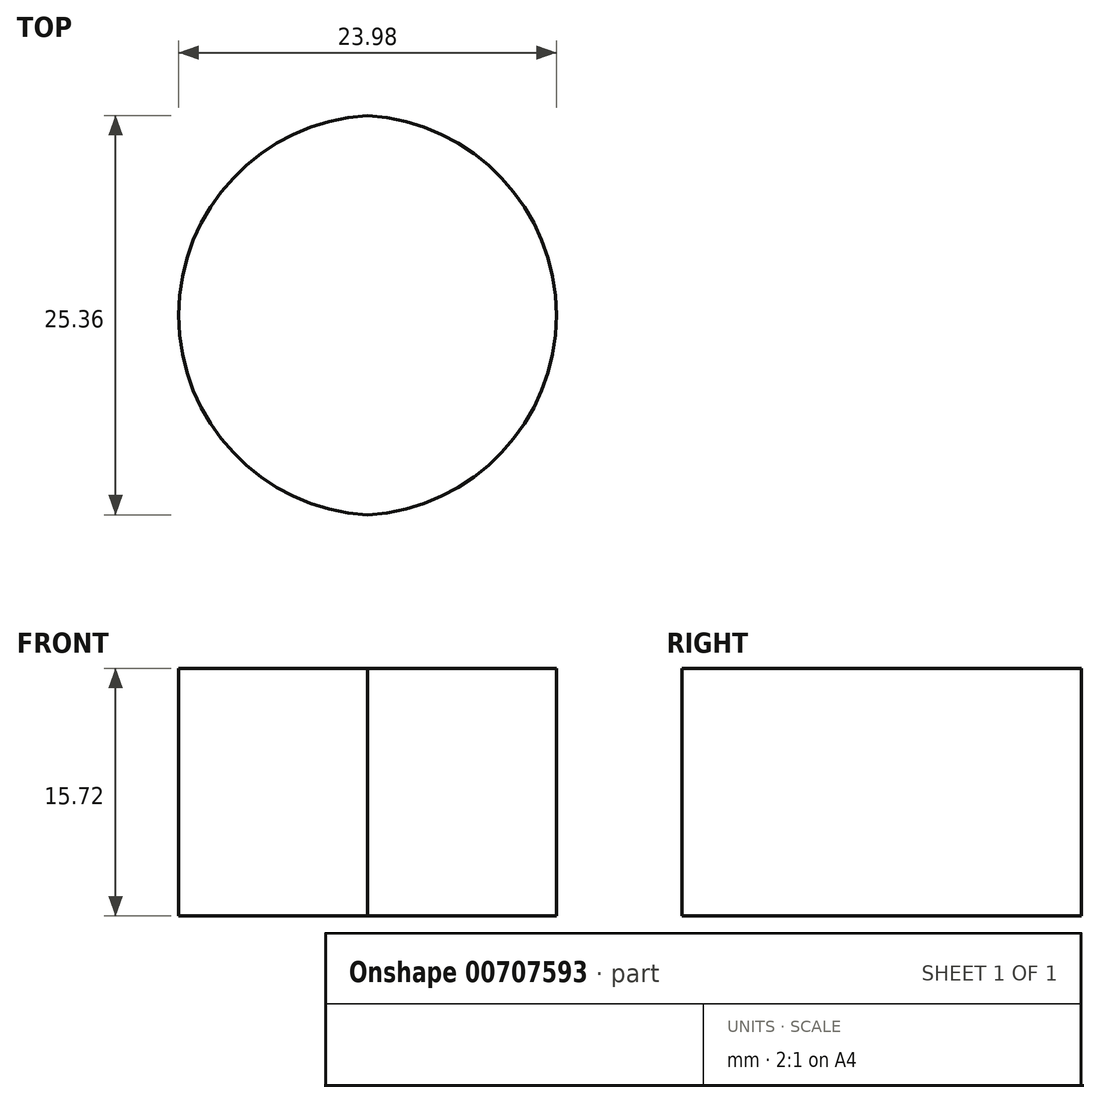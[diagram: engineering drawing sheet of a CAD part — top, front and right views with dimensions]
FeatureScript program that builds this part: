
annotation { "Feature Type Name" : "Feature", "Feature Type Description" : "" }
export const myFeature = defineFeature(function(context is Context, id is Id, definition is map)
    precondition{}
    {
        {
            var Q0;
            Q0=qCreatedBy(makeId("Front.planeOp"),FACE);
            var sketch = newSketch(context, id + "F0", { "sketchPlane" : qUnion([Q0])});
            skLineSegment(sketch, "E0", {"start": v(11.7, 8.56) * mm, "end": v(10.7, -7.18) * mm});
            skLineSegment(sketch, "E1", {"start": v(10.7, -7.18) * mm, "end": v(-10.6, 19) * mm});
            skLineSegment(sketch, "E2", {"start": v(-10.6, 19) * mm, "end": v(-7.8, 82.36) * mm});
            skFitSpline(sketch, "E3", {"points": [v(-7.8, 82.36) * mm, v(-7.24, 98.94) * mm, v(-6.59, 117.12) * mm, v(-5.83, 142.02) * mm, v(-5.45, 168.32) * mm, v(-5.52, 230.34) * mm, v(-6.26, 285.7) * mm, v(-7.2, 315.28) * mm, v(-8.95, 361.43) * mm, v(-10.4, 387.63) * mm, v(-13, 416.84) * mm, v(-15.01, 437.7) * mm, v(-21.29, 480.96) * mm, v(-27.2, 508.68) * mm, v(-28.7, 514.88) * mm], "startDerivative": vector(10.22, 308.11) * mm, "endDerivative": vector(-37.95, 155.7) * mm});
            skLineSegment(sketch, "E4", {"start": v(-28.7, 514.88) * mm, "end": v(-18.5, 504.49) * mm});
            skFitSpline(sketch, "E5", {"points": [v(-18.5, 504.49) * mm, v(-14.2, 494.72) * mm, v(-10.4, 483.17) * mm, v(-6.54, 469.9) * mm, v(-3.1, 457.05) * mm, v(-0.51, 445.6) * mm, v(1.47, 435.93) * mm, v(2.96, 426.2) * mm, v(4.35, 415.6) * mm, v(5.85, 403.15) * mm, v(7.18, 390.92) * mm, v(9.67, 369.53) * mm, v(11.56, 352.56) * mm, v(15.2, 318.42) * mm, v(18.03, 290.8) * mm, v(19.92, 265.34) * mm, v(21.72, 242.6) * mm, v(22.69, 220.79) * mm, v(23.65, 203.25) * mm, v(24.47, 178.85) * mm, v(25.08, 148.77) * mm, v(25.19, 106.94) * mm, v(24.82, 74.57) * mm, v(24.5, 42) * mm], "startDerivative": vector(138.63, -295.52) * mm, "endDerivative": vector(-5.12, -584.15) * mm});
            skFitSpline(sketch, "E6", {"points": [v(24.5, 42) * mm, v(16.7, 39) * mm, v(12.5, 33.24) * mm, v(9.61, 24.95) * mm, v(8.9, 16.91) * mm, v(10.33, 12.23) * mm, v(11.7, 8.56) * mm], "startDerivative": vector(-46.28, -12) * mm, "endDerivative": vector(10.21, -28.51) * mm});
            skFitSpline(sketch, "E7", {"points": [v(-10.6, 84.98) * mm, v(-8.5, 83) * mm, v(-6.65, 78.8) * mm, v(-5.89, 72.07) * mm, v(-5.76, 61.33) * mm, v(-5.64, 47.1) * mm, v(-5.9, 35.6) * mm, v(-6.47, 31.43) * mm, v(-6.34, 26.97) * mm, v(-4.57, 21.8) * mm, v(-2.21, 17.83) * mm, v(0, 15.05) * mm, v(2.28, 13.08) * mm, v(5.76, 11.32) * mm, v(8.69, 10.16) * mm, v(11.04, 8.9) * mm, v(12.38, 7.6) * mm, v(13.09, 5.99) * mm, v(12.89, 2.76) * mm, v(12.15, -3.9) * mm, v(11.7, -8.74) * mm, v(11.08, -13.22) * mm], "startDerivative": vector(59.9, -45.86) * mm, "endDerivative": vector(-14.62, -97.53) * mm});
            skLineSegment(sketch, "E8", {"start": v(11.08, -13.22) * mm, "end": v(11.08, -15.97) * mm});
            skLineSegment(sketch, "E9", {"start": v(11.08, -15.97) * mm, "end": v(-11.03, -15.97) * mm});
            skLineSegment(sketch, "E10", {"start": v(-11.03, -15.97) * mm, "end": v(-11.2, -13.29) * mm});
            skFitSpline(sketch, "E11", {"points": [v(-11.2, -13.29) * mm, v(-11.2, -11.84) * mm, v(-11.2, -5.52) * mm, v(-11.51, 1.49) * mm, v(-12.16, 4.66) * mm, v(-13.4, 9.05) * mm, v(-15.15, 13.55) * mm, v(-16.64, 17.33) * mm, v(-19.12, 23.61) * mm, v(-19.55, 26.56) * mm, v(-18.64, 31.28) * mm, v(-16.79, 35.33) * mm, v(-14.77, 40.57) * mm, v(-13.5, 46.17) * mm, v(-12.6, 53.4) * mm, v(-12.2, 59.96) * mm, v(-12.37, 65.97) * mm, v(-12.16, 73.91) * mm, v(-11.5, 81.04) * mm, v(-11.2, 84.64) * mm, v(-10.6, 84.98) * mm], "startDerivative": vector(-0.12, 43.3) * mm, "endDerivative": vector(35.61, 8.6) * mm});
            skFitSpline(sketch, "E12", {"points": [v(11.08, -13.22) * mm, v(15.57, -17.52) * mm, v(22.06, -24.41) * mm, v(29.6, -33.47) * mm, v(35.84, -41.56) * mm, v(40.17, -47.64) * mm, v(44.57, -55.74) * mm, v(47.94, -62.06) * mm, v(51.06, -67.51) * mm, v(52.42, -69.67) * mm, v(49.81, -81.38) * mm, v(45.5, -94.07) * mm, v(41.24, -106.63) * mm, v(36.2, -120.43) * mm, v(32.84, -130.03) * mm, v(29.35, -138.2) * mm, v(27.78, -142.23) * mm, v(23.27, -152.08) * mm, v(21.3, -154.75) * mm, v(16.02, -157.43) * mm, v(8.58, -160.03) * mm, v(4.77, -160.41) * mm, v(4.83, -154.75) * mm, v(8.26, -152.78) * mm, v(13.03, -150.3) * mm, v(16.97, -147.44) * mm, v(20.66, -141.85) * mm, v(25.37, -129.07) * mm, v(31.66, -108.36) * mm, v(36.51, -89.69) * mm, v(39.56, -77.02) * mm, v(39.75, -72.83) * mm, v(38.74, -67.42) * mm, v(35.21, -61.22) * mm, v(28.26, -50.55) * mm, v(23.02, -43.89) * mm, v(18.43, -38.21) * mm, v(13.22, -32.69) * mm, v(7.93, -27.32) * mm, v(6.6, -20.94) * mm, v(11.08, -13.22) * mm]});
            skLineSegment(sketch, "E13.bottom", {"start": v(-12.44, -13.29) * mm, "end": v(11.54, -13.29) * mm});
            skLineSegment(sketch, "E13.top", {"start": v(-12.44, -29.01) * mm, "end": v(11.54, -29.01) * mm});
            skLineSegment(sketch, "E13.left", {"start": v(-12.44, -13.29) * mm, "end": v(-12.44, -29.01) * mm});
            skLineSegment(sketch, "E13.right", {"start": v(11.54, -13.29) * mm, "end": v(11.54, -29.01) * mm});
            skLineSegment(sketch, "E14", {"start": v(0, -32.56) * mm, "end": v(0, -38.28) * mm});
            skFitSpline(sketch, "E15", {"points": [v(-10.75, -28.03) * mm, v(-9.93, -35.6) * mm, v(-9.25, -45.2) * mm, v(-8.25, -64.06) * mm, v(-7.6, -83.45) * mm, v(-7.55, -95.02) * mm, v(-7.45, -109.5) * mm, v(-7.73, -122.65) * mm, v(-8.29, -138.57) * mm, v(-9.14, -152.56) * mm, v(-9.03, -155.04) * mm], "startDerivative": vector(11.05, -94.6) * mm, "endDerivative": vector(4.37, -43.01) * mm});
            skLineSegment(sketch, "E16", {"start": v(-9.9, -153.6) * mm, "end": v(9.57, -153.6) * mm});
            skFitSpline(sketch, "E17.MirrorCS", {"points": [v(10.75, -28.03) * mm, v(9.93, -35.6) * mm, v(9.25, -45.2) * mm, v(8.25, -64.06) * mm, v(7.6, -83.45) * mm, v(7.55, -95.02) * mm, v(7.45, -109.5) * mm, v(7.73, -122.65) * mm, v(8.29, -138.57) * mm, v(9.14, -152.56) * mm, v(9.03, -155.04) * mm], "startDerivative": vector(-11.05, -94.6) * mm, "endDerivative": vector(-4.37, -43.01) * mm});
            skSolve(sketch);
        }
        {
            var Q0;
            {var subQ6=sQuery(id+"F0.wireOp",EDGE,"E10");Q0=makeQuery(id+"F0.imprint","IMPRINT",FACE,{"disambiguationData":[TD([[makeQuery(id+"F0.imprint","IMPRINT",EDGE,{"derivedFrom":subQ6}),1.0]])]});}
            var Q1;
            {var subQ7=sQuery(id+"F0.wireOp",EDGE,"E13.right");Q1=makeQuery(id+"F0.imprint","IMPRINT",FACE,{"disambiguationData":[TD([[makeQuery(id+"F0.imprint","IMPRINT",EDGE,{"derivedFrom":subQ7}),-1.0]])]});}
            var Q2;
            {var subQ0=sQuery(id+"F0.wireOp",EDGE,"E9");var subQ1=sQuery(id+"F0.wireOp",EDGE,"E8");var subQ2=makeQuery(id+"F0.imprint","INTERSECT",VERTEX,{"derivedFrom":[subQ1,subQ0]});Q2=makeQuery(id+"F0.imprint","IMPRINT",FACE,{"disambiguationData":[TD([[makeQuery(id+"F0.imprint","IMPRINT",EDGE,{"disambiguationData":[TD([[subQ2,1.0]])],"derivedFrom":subQ1}),-1.0]])]});}
            var Q3;
            {var subQ0=sQuery(id+"F0.wireOp",EDGE,"E10");Q3=makeQuery(id+"F0.imprint","IMPRINT",FACE,{"disambiguationData":[TD([[makeQuery(id+"F0.imprint","IMPRINT",EDGE,{"derivedFrom":subQ0}),-1.0]])]});}
            extrude(context, id + "F1", {"entities" : qUnion([Q0, Q1, Q2, Q3]), "endBound" : BoundingType.SYMMETRIC, "depth" : 25.4 * mm, "offsetDistance" : 25.4 * mm});
        }
        {
            var Q0;
            Q0=makeQuery(id+"F1.opExtrude","CAP_EDGE",EDGE,{"disambiguationData":[OSD([sQuery(id+"F0.wireOp",EDGE,"E13.right")])],"isStart":true});
            var Q1;
            Q1=makeQuery(id+"F1.opExtrude","CAP_EDGE",EDGE,{"disambiguationData":[OSD([sQuery(id+"F0.wireOp",EDGE,"E13.left")])],"isStart":true});
            var Q2;
            Q2=makeQuery(id+"F1.opExtrude","CAP_EDGE",EDGE,{"disambiguationData":[OSD([sQuery(id+"F0.wireOp",EDGE,"E13.left")])],"isStart":false});
            var Q3;
            Q3=makeQuery(id+"F1.opExtrude","CAP_EDGE",EDGE,{"disambiguationData":[OSD([sQuery(id+"F0.wireOp",EDGE,"E13.right")])],"isStart":false});
            fillet(context, id + "F2", {"entities" : qUnion([Q0, Q1, Q2, Q3]), "radius" : 12.7 * mm, "tangentPropagation" : true, "allowEdgeOverflow" : false});
        }
    });
